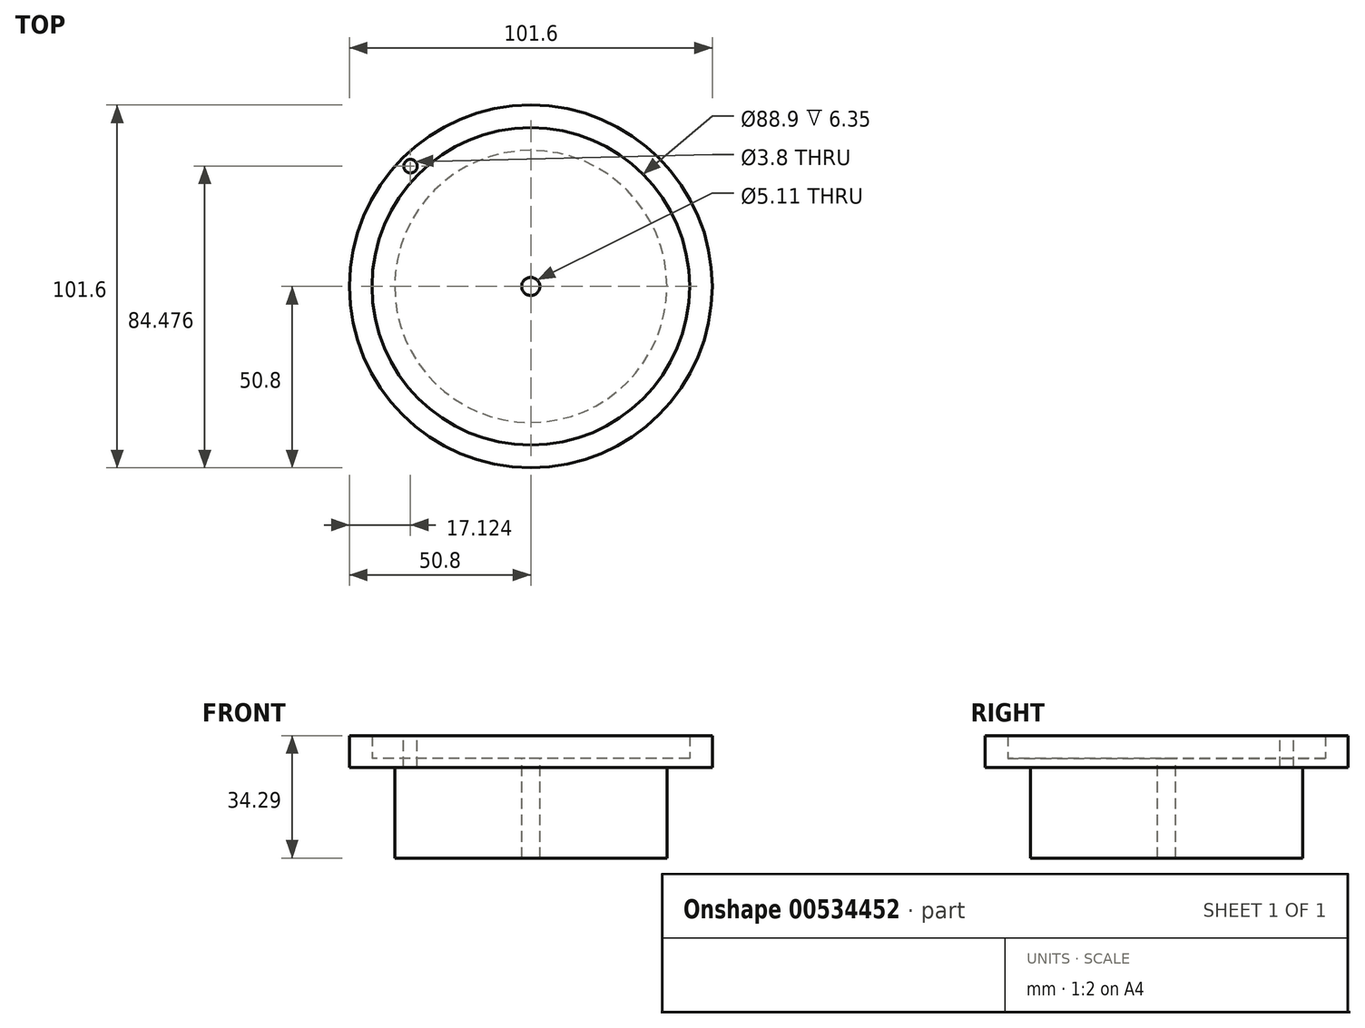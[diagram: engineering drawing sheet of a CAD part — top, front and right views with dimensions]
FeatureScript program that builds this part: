
annotation { "Feature Type Name" : "Feature", "Feature Type Description" : "" }
export const myFeature = defineFeature(function(context is Context, id is Id, definition is map)
    precondition{}
    {
        {
            var Q0;
            Q0=qCreatedBy(makeId("Top.planeOp"),FACE);
            var sketch = newSketch(context, id + "F0", { "sketchPlane" : qUnion([Q0])});
            skCircle(sketch, "E0", {"center": v(0, 0) * mm, "radius": 50.8 * mm});
            skSolve(sketch);
        }
        {
            var Q0;
            Q0=makeQuery(id+"F0.imprint","IMPRINT",FACE,{"disambiguationData":[TD([[makeQuery(id+"F0.imprint","IMPRINT",EDGE,{"derivedFrom":sQuery(id+"F0.wireOp",EDGE,"E0")}),1.0]])]});
            extrude(context, id + "F1", {"entities" : qUnion([Q0]), "depth" : 2.54 * mm, "offsetDistance" : 25.4 * mm});
        }
        {
            var Q0;
            Q0=makeQuery(id+"F1.opExtrude","CAP_FACE",FACE,{"disambiguationData":[OSD([sQuery(id+"F0.wireOp",EDGE,"E0")])],"isStart":false});
            var sketch = newSketch(context, id + "F2", { "sketchPlane" : qUnion([Q0])});
            skCircle(sketch, "E1", {"center": v(0, 0) * mm, "radius": 50.8 * mm});
            skCircle(sketch, "E2", {"center": v(0, 0) * mm, "radius": 44.45 * mm});
            skSolve(sketch);
        }
        {
            var Q0;
            Q0=makeQuery(id+"F2.imprint","IMPRINT",FACE,{"disambiguationData":[TD([[makeQuery(id+"F2.imprint","IMPRINT",EDGE,{"derivedFrom":sQuery(id+"F2.wireOp",EDGE,"E1")}),1.0]])]});
            extrude(context, id + "F3", {"entities" : qUnion([Q0]), "operationType" : NewBodyOperationType.ADD, "depth" : 6.35 * mm, "offsetDistance" : 25.4 * mm});
        }
        {
            var Q0;
            Q0=makeQuery(id+"F3.opExtrude","CAP_FACE",FACE,{"disambiguationData":[OSD([sQuery(id+"F2.wireOp",EDGE,"E1"),sQuery(id+"F2.wireOp",EDGE,"E2")])],"isStart":false});
            var sketch = newSketch(context, id + "F4", { "sketchPlane" : qUnion([Q0])});
            skPoint(sketch, "E3", {"position": v(-33.68, 33.68) * mm});
            skLineSegment(sketch, "E4", {"start": v(0, 44.45) * mm, "end": v(0, 0) * mm, "construction": true});
            skLineSegment(sketch, "E5", {"start": v(0, 0) * mm, "end": v(-33.68, 33.68) * mm, "construction": true});
            skSolve(sketch);
        }
        {
            var Q0;
            Q0=sQuery(id+"F4.wireOp",VERTEX,"E3");
            var Q1;
            Q1=makeQuery(id+"F1.opExtrude","SWEPT_BODY",BODY,{"disambiguationData":[OSD([sQuery(id+"F0.wireOp",EDGE,"E0")])]});
            hole(context, id + "F5", {"style" : HoleStyle.SIMPLE, "endStyle" : HoleEndStyle.THROUGH, "standardTappedOrClearance" : lookupTablePath({ "standard" : "ANSI", "engagement" : "75%", "pitch" : "24 tpi", "size" : "#10", "type" : "Tapped" }), "standardBlindInLast" : lookupTablePath({ "standard" : "ANSI", "engagement" : "75%", "pitch" : "24 tpi", "size" : "#10", "type" : "Tapped" }), "holeDiameter" : 3.8 * mm, "showTappedDepth" : true, "isTappedThrough" : true, "tappedDepth" : 12.7 * mm, "tapClearance" : 3, "locations" : qUnion([Q0]), "scope" : qUnion([Q1]), "majorDiameter" : 4.83 * mm});
        }
        {
            var Q0;
            Q0=makeQuery(id+"F1.opExtrude","CAP_FACE",FACE,{"disambiguationData":[OSD([sQuery(id+"F0.wireOp",EDGE,"E0")])],"isStart":false});
            var sketch = newSketch(context, id + "F6", { "sketchPlane" : qUnion([Q0])});
            skPoint(sketch, "E6", {"position": v(0, 0) * mm});
            skSolve(sketch);
        }
        {
            var Q0;
            Q0=sQuery(id+"F6.wireOp",VERTEX,"E6");
            var Q1;
            Q1=makeQuery(id+"F1.opExtrude","SWEPT_BODY",BODY,{"disambiguationData":[OSD([sQuery(id+"F0.wireOp",EDGE,"E0")])]});
            hole(context, id + "F7", {"style" : HoleStyle.SIMPLE, "endStyle" : HoleEndStyle.THROUGH, "standardTappedOrClearance" : lookupTablePath({ "standard" : "ANSI", "engagement" : "75%", "pitch" : "20 tpi", "size" : "1/4", "type" : "Tapped" }), "standardBlindInLast" : lookupTablePath({ "standard" : "ANSI", "engagement" : "75%", "pitch" : "20 tpi", "size" : "1/4", "type" : "Tapped" }), "holeDiameter" : 5.1 * mm, "showTappedDepth" : true, "isTappedThrough" : true, "tappedDepth" : 12.7 * mm, "tapClearance" : 3, "locations" : qUnion([Q0]), "scope" : qUnion([Q1]), "majorDiameter" : 6.35 * mm});
        }
        {
            var Q0;
            Q0=makeQuery(id+"F1.opExtrude","CAP_FACE",FACE,{"disambiguationData":[OSD([sQuery(id+"F0.wireOp",EDGE,"E0")])],"isStart":true});
            var sketch = newSketch(context, id + "F8", { "sketchPlane" : qUnion([Q0])});
            skCircle(sketch, "E7", {"center": v(0, 0) * mm, "radius": 38.1 * mm});
            skSolve(sketch);
        }
        {
            var Q0;
            Q0=makeQuery(id+"F8.imprint","IMPRINT",FACE,{"disambiguationData":[TD([[makeQuery(id+"F8.imprint","IMPRINT",EDGE,{"derivedFrom":sQuery(id+"F8.wireOp",EDGE,"E7")}),1.0]])]});
            var Q1;
            Q1=makeQuery(id+"F8.imprint","IMPRINT",FACE,{"disambiguationData":[TD([[makeQuery(id+"F8.imprint","IMPRINT",EDGE,{"derivedFrom":makeQuery(id+"F7.hole-0.boolean.opBoolean","INTERSECT",EDGE,{"derivedFrom":[makeQuery(id+"F1.opExtrude","CAP_FACE",FACE,{"disambiguationData":[OSD([sQuery(id+"F0.wireOp",EDGE,"E0")])],"isStart":true}),makeQuery(id+"F7.hole-0.opRevolve","SWEPT_FACE",FACE,{"disambiguationData":[OSD([sQuery(id+"F7.hole-0.sketch.wireOp",EDGE,"core_line_2")])]})]})}),1.0]])]});
            extrude(context, id + "F9", {"entities" : qUnion([Q0, Q1]), "operationType" : NewBodyOperationType.ADD, "depth" : 25.4 * mm, "offsetDistance" : 25.4 * mm});
        }
    });
